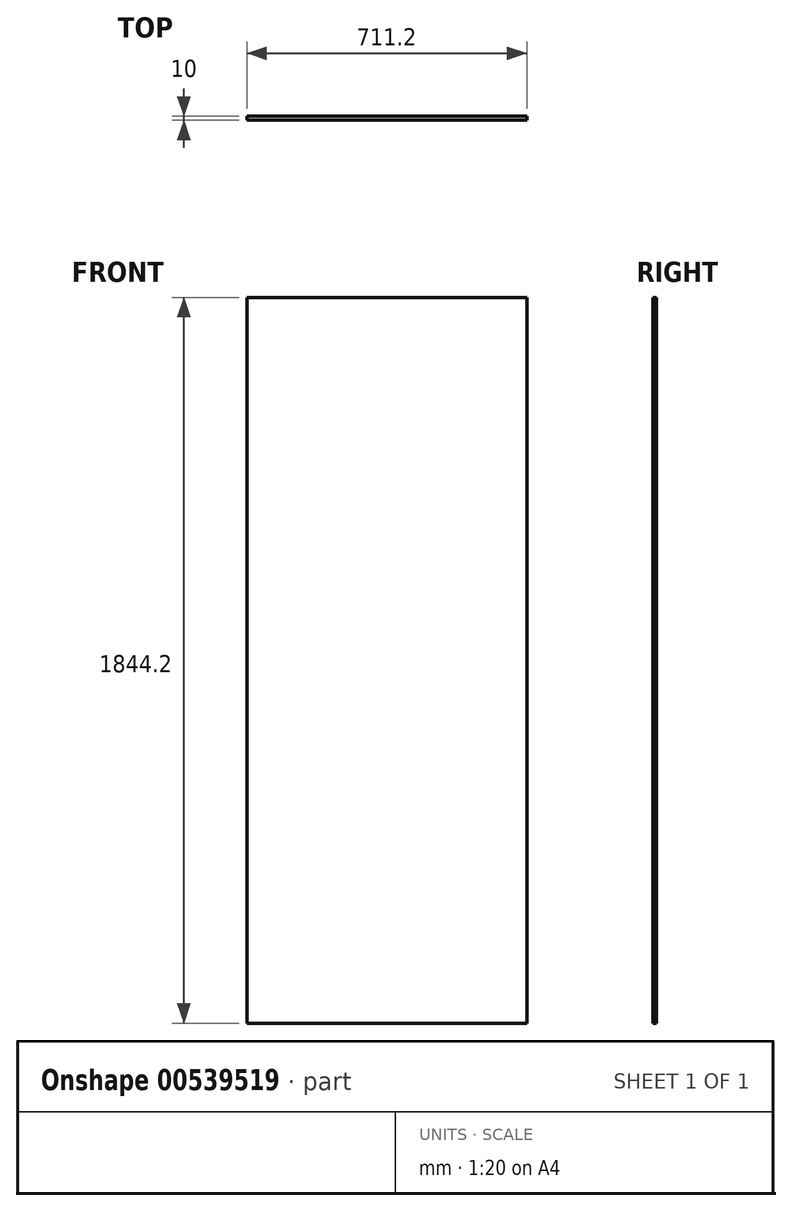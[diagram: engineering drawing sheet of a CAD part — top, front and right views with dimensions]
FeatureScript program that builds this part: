
annotation { "Feature Type Name" : "Feature", "Feature Type Description" : "" }
export const myFeature = defineFeature(function(context is Context, id is Id, definition is map)
    precondition{}
    {
        {
            var Q0;
            Q0=qCreatedBy(makeId("Front.planeOp"),FACE);
            var sketch = newSketch(context, id + "F0", { "sketchPlane" : qUnion([Q0])});
            skLineSegment(sketch, "E0.bottom", {"start": v(355.6, -922.1) * mm, "end": v(-355.6, -922.1) * mm});
            skLineSegment(sketch, "E0.top", {"start": v(355.6, 922.1) * mm, "end": v(-355.6, 922.1) * mm});
            skLineSegment(sketch, "E0.left", {"start": v(355.6, -922.1) * mm, "end": v(355.6, 922.1) * mm});
            skLineSegment(sketch, "E0.right", {"start": v(-355.6, -922.1) * mm, "end": v(-355.6, 922.1) * mm});
            skPoint(sketch, "E0.middle", {"position": v(0, 0) * mm});
            skSolve(sketch);
        }
        {
            var Q0;
            Q0=makeQuery(id+"F0.imprint","IMPRINT",FACE,{"disambiguationData":[TD([[makeQuery(id+"F0.imprint","IMPRINT",EDGE,{"derivedFrom":sQuery(id+"F0.wireOp",EDGE,"E0.bottom")}),-1.0]])]});
            extrude(context, id + "F1", {"entities" : qUnion([Q0]), "depth" : 10 * mm});
        }
    });
